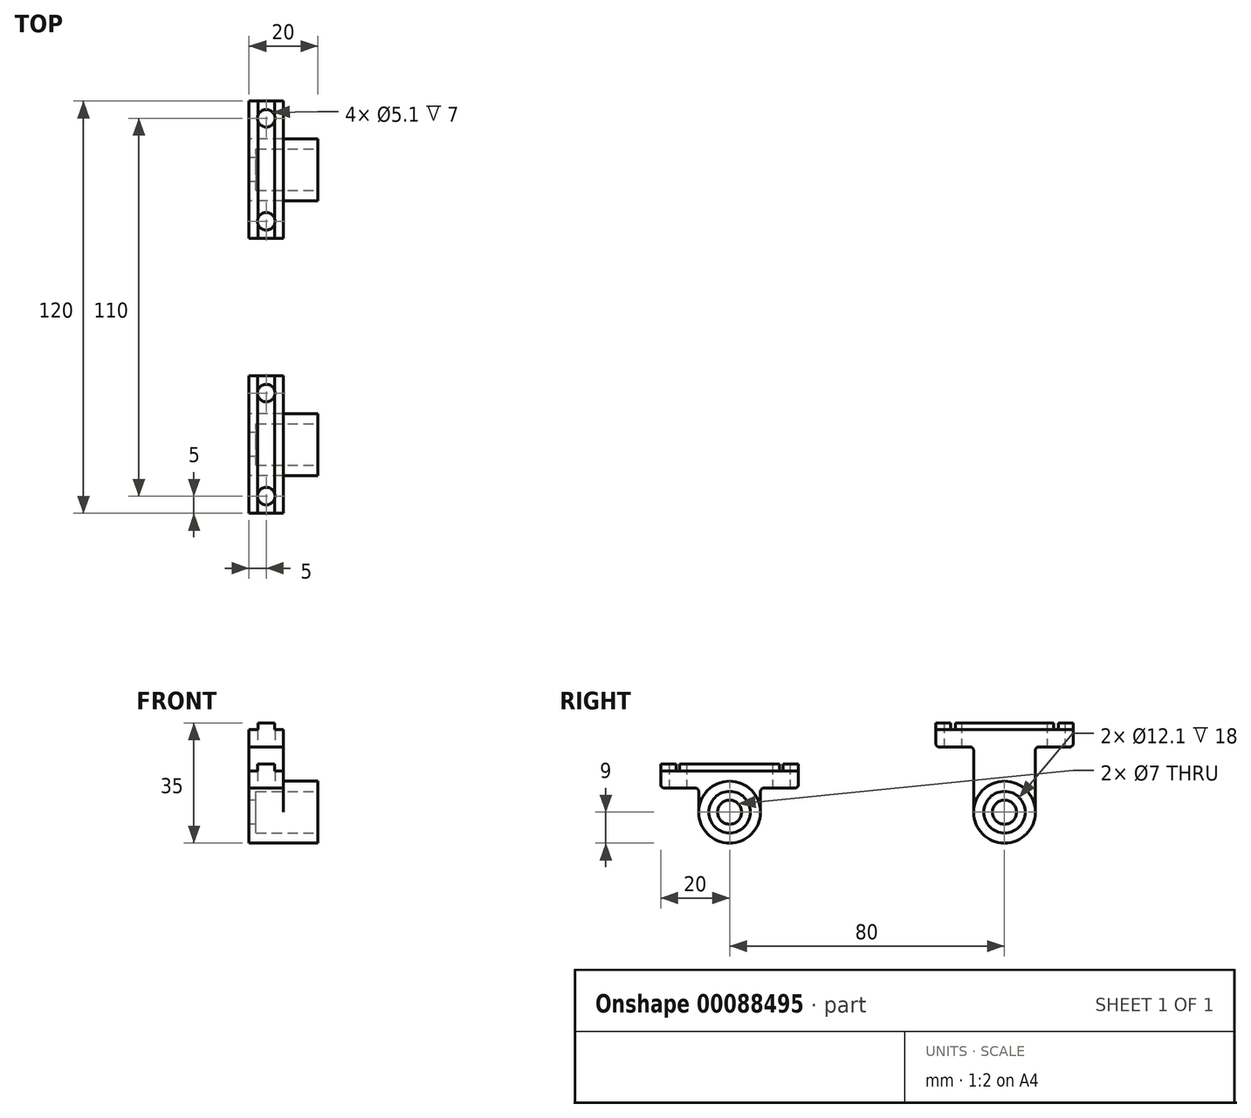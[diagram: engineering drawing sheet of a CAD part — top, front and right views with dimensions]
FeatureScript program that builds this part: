
annotation { "Feature Type Name" : "Feature", "Feature Type Description" : "" }
export const myFeature = defineFeature(function(context is Context, id is Id, definition is map)
    precondition{}
    {
        {
            var Q0;
            Q0=qCreatedBy(makeId("Right.planeOp"),FACE);
            var sketch = newSketch(context, id + "F0", { "sketchPlane" : qUnion([Q0])});
            skCircle(sketch, "E0", {"center": v(0, 0) * mm, "radius": 9 * mm});
            skSolve(sketch);
        }
        {
            var Q0;
            Q0 = qSketchRegion(id + "F0", true);
            extrude(context, id + "F1", {"entities" : qUnion([Q0]), "depth" : 20 * mm, "offsetDistance" : 25 * mm});
        }
        {
            var Q0;
            Q0=qCreatedBy(makeId("Front.planeOp"),FACE);
            cPlane(context, id + "F2", {"entities" : qUnion([Q0]), "cplaneType" : CPlaneType.OFFSET, "offset" : 40 * mm, "oppositeDirection" : true, "width" : 150 * mm, "height" : 150 * mm});
        }
        {
            var Q0;
            Q0=qCreatedBy(makeId("Front.planeOp"),FACE);
            var sketch = newSketch(context, id + "F3", { "sketchPlane" : qUnion([Q0])});
            skLineSegment(sketch, "E1.bottom", {"start": v(0, 24) * mm, "end": v(2.55, 24) * mm});
            skLineSegment(sketch, "E1.top", {"start": v(0, 0) * mm, "end": v(10, 0) * mm});
            skLineSegment(sketch, "E1.left", {"start": v(0, 24) * mm, "end": v(0, 0) * mm});
            skLineSegment(sketch, "E1.right", {"start": v(10, 24) * mm, "end": v(10, 0) * mm});
            skLineSegment(sketch, "E2.bottom", {"start": v(2.55, 26) * mm, "end": v(7.45, 26) * mm});
            skLineSegment(sketch, "E2.left", {"start": v(2.55, 26) * mm, "end": v(2.55, 24) * mm});
            skLineSegment(sketch, "E2.right", {"start": v(7.45, 26) * mm, "end": v(7.45, 24) * mm});
            skPoint(sketch, "E2.middle", {"position": v(5, 24) * mm});
            skLineSegment(sketch, "E3.trimOffspring", {"start": v(7.45, 24) * mm, "end": v(10, 24) * mm});
            skSolve(sketch);
        }
        {
            var Q0;
            Q0 = qSketchRegion(id + "F3", true);
            extrude(context, id + "F4", {"entities" : qUnion([Q0]), "operationType" : NewBodyOperationType.ADD, "endBound" : BoundingType.SYMMETRIC, "depth" : 40 * mm});
        }
        {
            var Q0;
            Q0=makeQuery(id+"F1.opExtrude","SWEPT_BODY",BODY,{"disambiguationData":[OSD([sQuery(id+"F0.wireOp",EDGE,"E0")])]});
            var Q1;
            Q1=qCreatedBy(id+"F2.planeOp",FACE);
            mirror(context, id + "F5", {"entities" : qUnion([Q0]), "mirrorPlane" : qUnion([Q1])});
        }
        {
            var Q0;
            Q0=makeQuery(id+"F4.opExtrude","CAP_FACE",FACE,{"disambiguationData":[OSD([sQuery(id+"F3.wireOp",EDGE,"E1.bottom"),sQuery(id+"F3.wireOp",EDGE,"E1.top"),sQuery(id+"F3.wireOp",EDGE,"E1.left"),sQuery(id+"F3.wireOp",EDGE,"E1.right"),sQuery(id+"F3.wireOp",EDGE,"E2.bottom"),sQuery(id+"F3.wireOp",EDGE,"E2.left"),sQuery(id+"F3.wireOp",EDGE,"E2.right"),sQuery(id+"F3.wireOp",EDGE,"E3.trimOffspring")])],"isStart":false});
            var sketch = newSketch(context, id + "F6", { "sketchPlane" : qUnion([Q0])});
            skLineSegment(sketch, "E4", {"start": v(0, 12) * mm, "end": v(2.5, 12) * mm});
            skLineSegment(sketch, "E5", {"start": v(2.5, 12) * mm, "end": v(2.5, 14) * mm});
            skLineSegment(sketch, "E6", {"start": v(2.5, 14) * mm, "end": v(7.5, 14) * mm});
            skLineSegment(sketch, "E7", {"start": v(7.5, 14) * mm, "end": v(7.5, 12) * mm});
            skLineSegment(sketch, "E8", {"start": v(7.5, 12) * mm, "end": v(10, 12) * mm});
            skLineSegment(sketch, "E9", {"start": v(0, 12) * mm, "end": v(0, 26) * mm});
            skLineSegment(sketch, "E10", {"start": v(0, 26) * mm, "end": v(10, 26) * mm});
            skLineSegment(sketch, "E11", {"start": v(10, 26) * mm, "end": v(10, 12) * mm});
            skSolve(sketch);
        }
        {
            var Q0;
            Q0 = qSketchRegion(id + "F6", true);
            extrude(context, id + "F7", {"entities" : qUnion([Q0]), "operationType" : NewBodyOperationType.REMOVE, "oppositeDirection" : true, "depth" : 40 * mm});
        }
        {
            var Q0;
            Q0=makeQuery(id+"F4.opExtrude","SWEPT_FACE",FACE,{"disambiguationData":[OSD([sQuery(id+"F3.wireOp",EDGE,"E1.right")])]});
            var sketch = newSketch(context, id + "F8", { "sketchPlane" : qUnion([Q0])});
            skLineSegment(sketch, "E12", {"start": v(-19, 7) * mm, "end": v(-10, 7) * mm});
            skLineSegment(sketch, "E13", {"start": v(-9, 6) * mm, "end": v(-9, 0) * mm});
            skPoint(sketch, "E14.visualSharp", {"position": v(-9, 7) * mm});
            skArc(sketch, "E14.filletArc", {"start": v(-9, 6) * mm, "mid": v(-9.3, 6.7) * mm, "end": v(-10, 7) * mm});
            skLineSegment(sketch, "E15", {"start": v(0, 0) * mm, "end": v(0, 6.2) * mm, "construction": true});
            skLineSegment(sketch, "E16", {"start": v(-20, 0) * mm, "end": v(-20, 8) * mm});
            skPoint(sketch, "E17.visualSharp", {"position": v(-20, 7) * mm});
            skArc(sketch, "E17.filletArc", {"start": v(-20, 8) * mm, "mid": v(-19.7, 7.3) * mm, "end": v(-19, 7) * mm});
            skLineSegment(sketch, "E18.MirrorCS", {"start": v(9, 6) * mm, "end": v(9, 0) * mm});
            skArc(sketch, "E19.MirrorCS", {"start": v(9, 6) * mm, "mid": v(9.3, 6.7) * mm, "end": v(10, 7) * mm});
            skLineSegment(sketch, "E20.MirrorCS", {"start": v(19, 7) * mm, "end": v(10, 7) * mm});
            skArc(sketch, "E21.MirrorCS", {"start": v(20, 8) * mm, "mid": v(19.7, 7.3) * mm, "end": v(19, 7) * mm});
            skLineSegment(sketch, "E22.MirrorCS", {"start": v(20, 0) * mm, "end": v(20, 8) * mm});
            skLineSegment(sketch, "E23", {"start": v(-20, 0) * mm, "end": v(-9, 0) * mm});
            skLineSegment(sketch, "E24.MirrorCS", {"start": v(20, 0) * mm, "end": v(9, 0) * mm});
            skLineSegment(sketch, "E25", {"start": v(60, 20) * mm, "end": v(60, 0) * mm});
            skLineSegment(sketch, "E26", {"start": v(60, 0) * mm, "end": v(71, 0) * mm});
            skLineSegment(sketch, "E27", {"start": v(71, 0) * mm, "end": v(71, 18) * mm});
            skLineSegment(sketch, "E28", {"start": v(70, 19) * mm, "end": v(61, 19) * mm});
            skArc(sketch, "E29", {"start": v(60, 20) * mm, "mid": v(60.3, 19.3) * mm, "end": v(61, 19) * mm});
            skPoint(sketch, "E30.visualSharp", {"position": v(71, 19) * mm});
            skArc(sketch, "E30.filletArc", {"start": v(71, 18) * mm, "mid": v(70.7, 18.7) * mm, "end": v(70, 19) * mm});
            skLineSegment(sketch, "E31", {"start": v(100, 20) * mm, "end": v(100, 0) * mm});
            skLineSegment(sketch, "E32", {"start": v(100, 0) * mm, "end": v(89, 0) * mm});
            skLineSegment(sketch, "E33", {"start": v(89, 0) * mm, "end": v(89, 18) * mm});
            skLineSegment(sketch, "E34", {"start": v(90, 19) * mm, "end": v(99, 19) * mm});
            skArc(sketch, "E35", {"start": v(99, 19) * mm, "mid": v(99.7, 19.3) * mm, "end": v(100, 20) * mm});
            skPoint(sketch, "E36.visualSharp", {"position": v(89, 19) * mm});
            skArc(sketch, "E36.filletArc", {"start": v(90, 19) * mm, "mid": v(89.3, 18.7) * mm, "end": v(89, 18) * mm});
            skSolve(sketch);
        }
        {
            var Q0;
            Q0 = qSketchRegion(id + "F8", true);
            extrude(context, id + "F9", {"entities" : qUnion([Q0]), "operationType" : NewBodyOperationType.REMOVE, "oppositeDirection" : true, "depth" : 25 * mm});
        }
        {
            var Q0;
            Q0=makeQuery(id+"F1.opExtrude","CAP_FACE",FACE,{"disambiguationData":[OSD([sQuery(id+"F0.wireOp",EDGE,"E0")])],"isStart":false});
            var sketch = newSketch(context, id + "F10", { "sketchPlane" : qUnion([Q0])});
            skCircle(sketch, "E37", {"center": v(0, 0) * mm, "radius": 6.05 * mm});
            skCircle(sketch, "E38", {"center": v(80, 0) * mm, "radius": 6.05 * mm});
            skSolve(sketch);
        }
        {
            var Q0;
            Q0 = qSketchRegion(id + "F10", true);
            extrude(context, id + "F11", {"entities" : qUnion([Q0]), "operationType" : NewBodyOperationType.REMOVE, "oppositeDirection" : true, "depth" : 18 * mm});
        }
        {
            var Q0;
            Q0=makeQuery(id+"F1.opExtrude","CAP_FACE",FACE,{"disambiguationData":[OSD([sQuery(id+"F0.wireOp",EDGE,"E0")])],"isStart":true});
            var sketch = newSketch(context, id + "F12", { "sketchPlane" : qUnion([Q0])});
            skCircle(sketch, "E39", {"center": v(0, 0) * mm, "radius": 3.5 * mm});
            skCircle(sketch, "E40", {"center": v(-80, 0) * mm, "radius": 3.5 * mm});
            skSolve(sketch);
        }
        {
            var Q0;
            Q0 = qSketchRegion(id + "F12", true);
            extrude(context, id + "F13", {"entities" : qUnion([Q0]), "operationType" : NewBodyOperationType.REMOVE, "oppositeDirection" : true, "depth" : 25 * mm});
        }
        {
            var Q0;
            Q0=makeQuery(id+"F9.boolean.opBoolean","COPY",FACE,{"derivedFrom":makeQuery(id+"F9.opExtrude","SWEPT_FACE",FACE,{"disambiguationData":[OSD([sQuery(id+"F8.wireOp",EDGE,"E12")])]})});
            var sketch = newSketch(context, id + "F14", { "sketchPlane" : qUnion([Q0])});
            skCircle(sketch, "E41", {"center": v(5, 15) * mm, "radius": 2.55 * mm});
            skPoint(sketch, "E41.centerSnap0", {"position": v(5, 19) * mm});
            skCircle(sketch, "E42", {"center": v(5, -15) * mm, "radius": 2.55 * mm});
            skLineSegment(sketch, "E43", {"start": v(-16.55, -40) * mm, "end": v(11.7, -40) * mm, "construction": true});
            skCircle(sketch, "E44.MirrorC", {"center": v(5, -65) * mm, "radius": 2.55 * mm});
            skCircle(sketch, "E45.MirrorC", {"center": v(5, -95) * mm, "radius": 2.55 * mm});
            skSolve(sketch);
        }
        {
            var Q0;
            Q0 = qSketchRegion(id + "F14", true);
            extrude(context, id + "F15", {"entities" : qUnion([Q0]), "operationType" : NewBodyOperationType.REMOVE, "endBound" : BoundingType.THROUGH_ALL, "oppositeDirection" : true, "depth" : 25 * mm});
        }
    });
